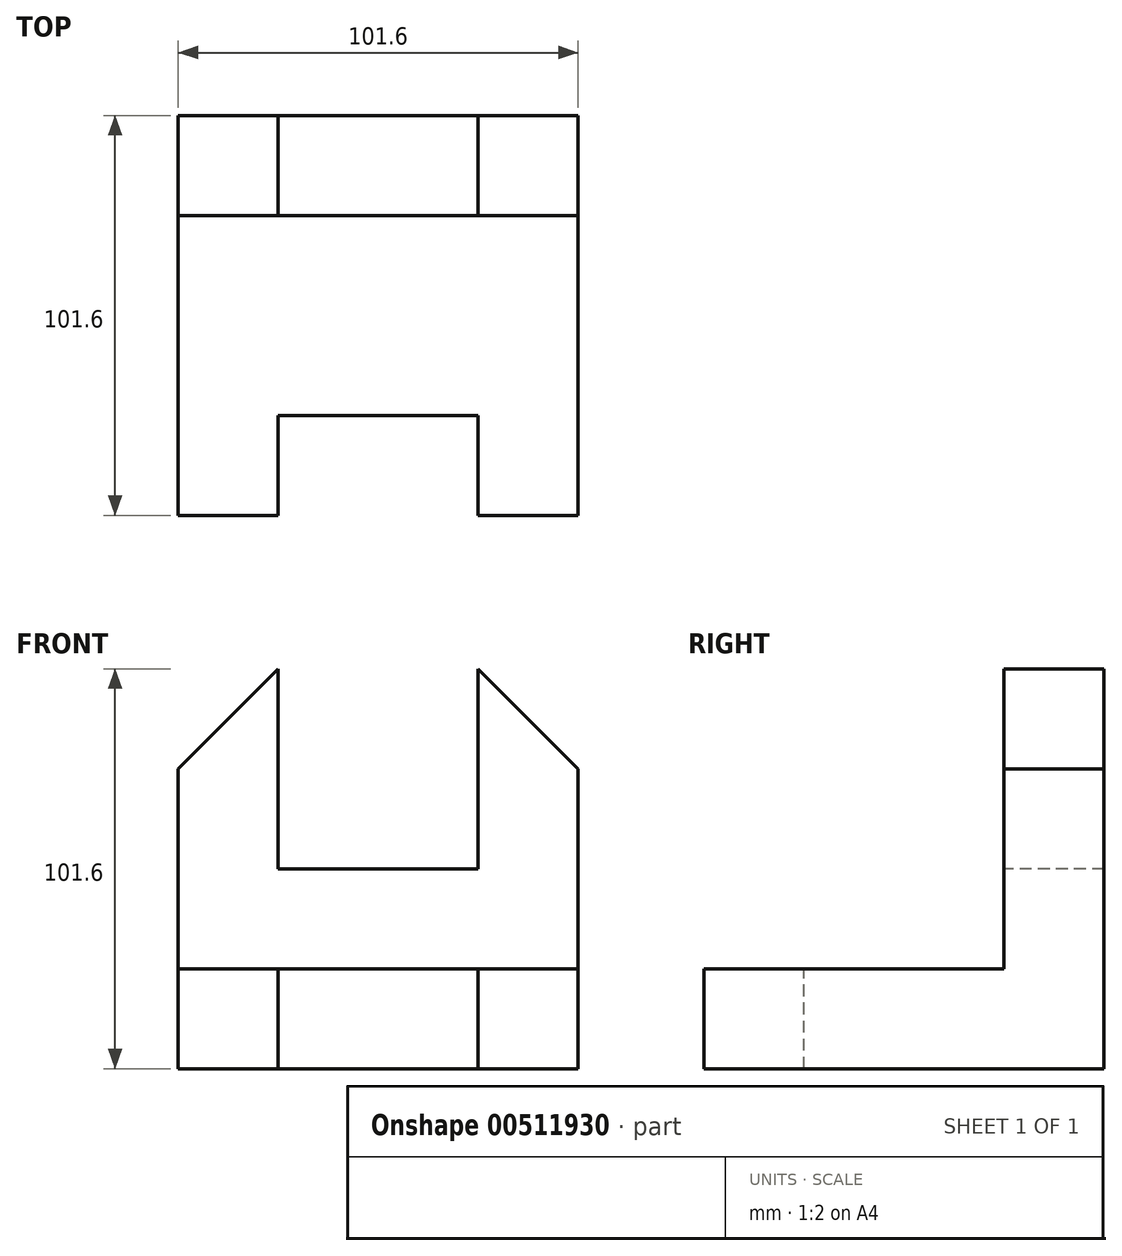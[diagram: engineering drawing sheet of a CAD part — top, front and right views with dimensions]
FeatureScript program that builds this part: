
annotation { "Feature Type Name" : "Feature", "Feature Type Description" : "" }
export const myFeature = defineFeature(function(context is Context, id is Id, definition is map)
    precondition{}
    {
        {
            var Q0;
            Q0=qCreatedBy(makeId("Front.planeOp"),FACE);
            var sketch = newSketch(context, id + "F0", { "sketchPlane" : qUnion([Q0])});
            skLineSegment(sketch, "E0.bottom", {"start": v(0, 0) * mm, "end": v(-101.6, 0) * mm});
            skLineSegment(sketch, "E0.top", {"start": v(0, 101.6) * mm, "end": v(-101.6, 101.6) * mm});
            skLineSegment(sketch, "E0.left", {"start": v(0, 0) * mm, "end": v(0, 101.6) * mm});
            skLineSegment(sketch, "E0.right", {"start": v(-101.6, 0) * mm, "end": v(-101.6, 101.6) * mm});
            skSolve(sketch);
        }
        {
            var Q0;
            Q0=makeQuery(id+"F0.imprint","IMPRINT",FACE,{"disambiguationData":[TD([[makeQuery(id+"F0.imprint","IMPRINT",EDGE,{"derivedFrom":sQuery(id+"F0.wireOp",EDGE,"E0.bottom")}),-1.0]])]});
            extrude(context, id + "F1", {"entities" : qUnion([Q0]), "depth" : 101.6 * mm});
        }
        {
            var Q0;
            Q0=makeQuery(id+"F1.opExtrude","SWEPT_FACE",FACE,{"disambiguationData":[OSD([sQuery(id+"F0.wireOp",EDGE,"E0.left")])]});
            var sketch = newSketch(context, id + "F2", { "sketchPlane" : qUnion([Q0])});
            skLineSegment(sketch, "E1.bottom", {"start": v(-101.6, 101.6) * mm, "end": v(-25.4, 101.6) * mm});
            skLineSegment(sketch, "E1.top", {"start": v(-101.6, 25.4) * mm, "end": v(-25.4, 25.4) * mm});
            skLineSegment(sketch, "E1.left", {"start": v(-101.6, 101.6) * mm, "end": v(-101.6, 25.4) * mm});
            skLineSegment(sketch, "E1.right", {"start": v(-25.4, 101.6) * mm, "end": v(-25.4, 25.4) * mm});
            skSolve(sketch);
        }
        {
            var Q0;
            Q0=makeQuery(id+"F2.imprint","IMPRINT",FACE,{"disambiguationData":[TD([[makeQuery(id+"F2.imprint","IMPRINT",EDGE,{"derivedFrom":sQuery(id+"F2.wireOp",EDGE,"E1.bottom")}),-1.0]])]});
            extrude(context, id + "F3", {"entities" : qUnion([Q0]), "operationType" : NewBodyOperationType.REMOVE, "oppositeDirection" : true, "depth" : 123.95 * mm});
        }
        {
            var Q0;
            Q0=makeQuery(id+"F3.boolean.opBoolean","COPY",FACE,{"derivedFrom":makeQuery(id+"F3.opExtrude","SWEPT_FACE",FACE,{"disambiguationData":[OSD([sQuery(id+"F2.wireOp",EDGE,"E1.right")])]})});
            var sketch = newSketch(context, id + "F4", { "sketchPlane" : qUnion([Q0])});
            skLineSegment(sketch, "E2", {"start": v(-101.6, 101.6) * mm, "end": v(-76.2, 101.6) * mm});
            skLineSegment(sketch, "E3", {"start": v(-76.2, 101.6) * mm, "end": v(-76.2, 50.8) * mm});
            skLineSegment(sketch, "E4", {"start": v(-76.2, 50.8) * mm, "end": v(-25.4, 50.8) * mm});
            skLineSegment(sketch, "E5", {"start": v(-25.4, 50.8) * mm, "end": v(-25.4, 101.6) * mm});
            skSolve(sketch);
        }
        {
            var Q0;
            {var subQ0=sQuery(id+"F4.wireOp",EDGE,"E3");Q0=makeQuery(id+"F4.imprint","IMPRINT",FACE,{"disambiguationData":[TD([[makeQuery(id+"F4.imprint","IMPRINT",EDGE,{"derivedFrom":subQ0}),1.0]])]});}
            extrude(context, id + "F5", {"entities" : qUnion([Q0]), "operationType" : NewBodyOperationType.REMOVE, "oppositeDirection" : true, "depth" : 25.4 * mm});
        }
        {
            var Q0;
            Q0=makeQuery(id+"F3.boolean.opBoolean","COPY",FACE,{"derivedFrom":makeQuery(id+"F3.opExtrude","SWEPT_FACE",FACE,{"disambiguationData":[OSD([sQuery(id+"F2.wireOp",EDGE,"E1.top")])]})});
            var sketch = newSketch(context, id + "F6", { "sketchPlane" : qUnion([Q0])});
            skLineSegment(sketch, "E6", {"start": v(-101.6, -101.6) * mm, "end": v(-76.2, -101.6) * mm});
            skLineSegment(sketch, "E7", {"start": v(-76.2, -101.6) * mm, "end": v(-76.2, -76.2) * mm});
            skLineSegment(sketch, "E8", {"start": v(-76.2, -76.2) * mm, "end": v(-25.4, -76.2) * mm});
            skLineSegment(sketch, "E9", {"start": v(-25.4, -76.2) * mm, "end": v(-25.4, -101.6) * mm});
            skSolve(sketch);
        }
        {
            var Q0;
            {var subQ0=sQuery(id+"F6.wireOp",EDGE,"E7");Q0=makeQuery(id+"F6.imprint","IMPRINT",FACE,{"disambiguationData":[TD([[makeQuery(id+"F6.imprint","IMPRINT",EDGE,{"derivedFrom":subQ0}),-1.0]])]});}
            extrude(context, id + "F7", {"entities" : qUnion([Q0]), "operationType" : NewBodyOperationType.REMOVE, "oppositeDirection" : true, "depth" : 25.4 * mm});
        }
        {
            var Q0;
            Q0=makeQuery(id+"F3.boolean.opBoolean","COPY",FACE,{"derivedFrom":makeQuery(id+"F3.opExtrude","SWEPT_FACE",FACE,{"disambiguationData":[OSD([sQuery(id+"F2.wireOp",EDGE,"E1.right")])]})});
            var sketch = newSketch(context, id + "F8", { "sketchPlane" : qUnion([Q0])});
            skLineSegment(sketch, "E10", {"start": v(-101.6, 101.6) * mm, "end": v(-101.6, 76.2) * mm});
            skLineSegment(sketch, "E11", {"start": v(-101.6, 76.2) * mm, "end": v(-76.2, 76.2) * mm});
            skLineSegment(sketch, "E12", {"start": v(-76.2, 76.2) * mm, "end": v(-101.6, 76.2) * mm});
            skLineSegment(sketch, "E13", {"start": v(-101.6, 76.2) * mm, "end": v(-76.2, 101.6) * mm});
            skSolve(sketch);
        }
        {
            var Q0;
            Q0=makeQuery(id+"F8.imprint","IMPRINT",FACE,{"disambiguationData":[TD([[makeQuery(id+"F8.imprint","IMPRINT",EDGE,{"derivedFrom":sQuery(id+"F8.wireOp",EDGE,"E10")}),-1.0]])]});
            extrude(context, id + "F9", {"entities" : qUnion([Q0]), "operationType" : NewBodyOperationType.REMOVE, "oppositeDirection" : true, "depth" : 25.4 * mm});
        }
        {
            var Q0;
            Q0=makeQuery(id+"F3.boolean.opBoolean","COPY",FACE,{"derivedFrom":makeQuery(id+"F3.opExtrude","SWEPT_FACE",FACE,{"disambiguationData":[OSD([sQuery(id+"F2.wireOp",EDGE,"E1.right")])]})});
            var sketch = newSketch(context, id + "F10", { "sketchPlane" : qUnion([Q0])});
            skLineSegment(sketch, "E14", {"start": v(-25.4, 101.6) * mm, "end": v(-25.4, 76.2) * mm});
            skLineSegment(sketch, "E15", {"start": v(-25.4, 76.2) * mm, "end": v(0, 76.2) * mm});
            skLineSegment(sketch, "E16", {"start": v(0, 76.2) * mm, "end": v(-25.4, 101.6) * mm});
            skSolve(sketch);
        }
        {
            var Q0;
            {var subQ0=sQuery(id+"F10.wireOp",EDGE,"E16");Q0=makeQuery(id+"F10.imprint","IMPRINT",FACE,{"disambiguationData":[TD([[makeQuery(id+"F10.imprint","IMPRINT",EDGE,{"derivedFrom":subQ0}),-1.0]])]});}
            extrude(context, id + "F11", {"entities" : qUnion([Q0]), "operationType" : NewBodyOperationType.REMOVE, "oppositeDirection" : true, "depth" : 25.4 * mm});
        }
    });
